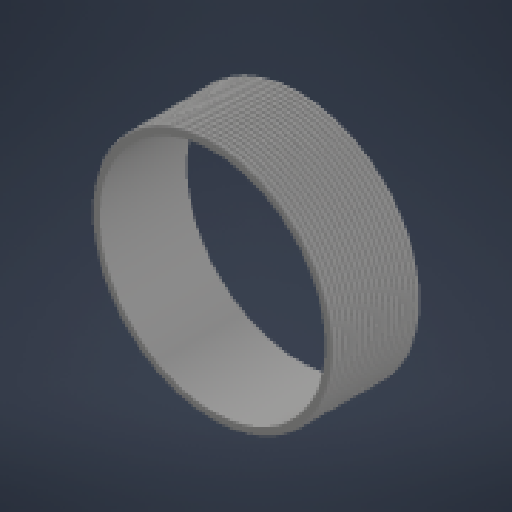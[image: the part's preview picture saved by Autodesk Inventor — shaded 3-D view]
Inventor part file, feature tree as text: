
AUTODESK INVENTOR PART (.ipt)
format: ipt  version: 2024.2 (Build 282272000, 272)  size: 282,112 bytes
history: native  units: in
note: dims shown in document units (in); Inventor stores cm internally (conversion verified against a paired STEP export)
features: reference x4, sketch x3, extrude x2, other x2, revolve x1, fillet x1
ambient origin geometry x8: Origin, YZ Plane, XZ Plane, XY Plane, X Axis, Y Axis, Z Axis, Center Point
bodies: Body1 (feature_tree)
feature tree (13):
  revolve  "Revolution1"  [1 undecoded]
  extrude  "Extrusion3"  Depth=0.3937in
  fillet  "Fillet1"  Radius=0.028in
  extrude  "Extrusion4"  Depth=0.1in
  sketch  "Sketch4"  dims[d12=1.024in d13=1.3173in]
  sketch  "Sketch5"  dims[d14=0.072in d16=6.6929in d18=0.06in d19=0.3937in d21=1.0in d25=0.028in]
  sketch  "Sketch6"  dims[d26=0.0017in d27=0.004in d28=0.0in d29=360.0deg d30=0.4in d31=0.8in d32=0.0in d33=0.75in d34=0.375in d35=0.0in d36=2.3622in d38=360.0deg d40=0.0in d41=0.0in d42=0.1in d43=0.5591in d44=0.0in d45=0.0in d46=0.1693in d47=0.1693in d48=0.1693in d49=0.1693in d3=0.5in d4=0.0344in d5=0.5in d6=0.0344in]
  reference  "Reference1"
  reference  "Reference2"
  reference  "Reference3"
  reference  "Reference4"
  other  "Assembly1"
  other  "Part19:1"
note: 1 required parameter value undecoded (feature->parameter linkage not recoverable at this tier; creation-order binding heuristic only, values carry confidence <= 0.55)
